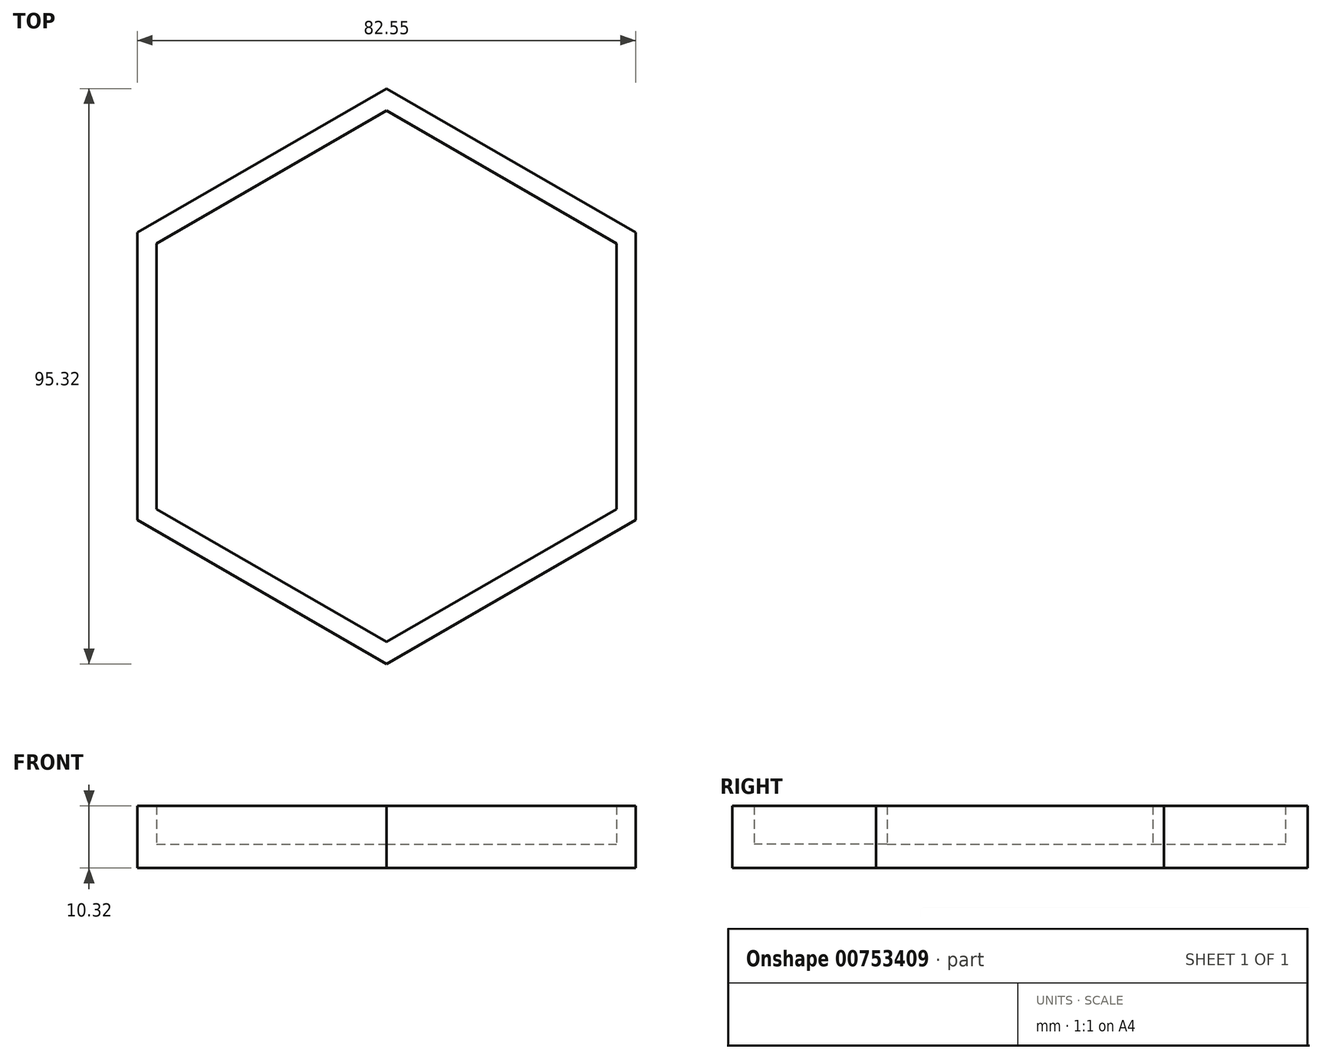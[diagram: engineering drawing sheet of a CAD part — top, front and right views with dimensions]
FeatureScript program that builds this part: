
annotation { "Feature Type Name" : "Feature", "Feature Type Description" : "" }
export const myFeature = defineFeature(function(context is Context, id is Id, definition is map)
    precondition{}
    {
        {
            var Q0;
            Q0=qCreatedBy(makeId("Top.planeOp"),FACE);
            var sketch = newSketch(context, id + "F0", { "sketchPlane" : qUnion([Q0])});
            skCircle(sketch, "E0.cCircle", {"center": v(0, 0) * mm, "radius": 41.28 * mm, "construction": true});
            skLineSegment(sketch, "E0.0", {"start": v(-41.28, -23.83) * mm, "end": v(-41.28, 23.83) * mm});
            skLineSegment(sketch, "E0.1", {"start": v(-41.28, 23.83) * mm, "end": v(0, 47.66) * mm});
            skLineSegment(sketch, "E0.2", {"start": v(0, 47.66) * mm, "end": v(41.28, 23.83) * mm});
            skLineSegment(sketch, "E0.3", {"start": v(41.27, 23.83) * mm, "end": v(41.28, -23.83) * mm});
            skLineSegment(sketch, "E0.4", {"start": v(41.28, -23.83) * mm, "end": v(0, -47.66) * mm});
            skLineSegment(sketch, "E0.5", {"start": v(0, -47.66) * mm, "end": v(-41.27, -23.83) * mm});
            skPoint(sketch, "E0.0.midPoint", {"position": v(-41.28, 0) * mm});
            skSolve(sketch);
        }
        {
            var Q0;
            Q0=makeQuery(id+"F0.imprint","IMPRINT",FACE,{"disambiguationData":[TD([[makeQuery(id+"F0.imprint","IMPRINT",EDGE,{"derivedFrom":sQuery(id+"F0.wireOp",EDGE,"E0.0")}),-1.0]])]});
            extrude(context, id + "F1", {"entities" : qUnion([Q0]), "depth" : 3.97 * mm, "offsetDistance" : 25.4 * mm});
        }
        {
            var Q0;
            Q0=makeQuery(id+"F1.opExtrude","CAP_FACE",FACE,{"disambiguationData":[OSD([sQuery(id+"F0.wireOp",EDGE,"E0.0"),sQuery(id+"F0.wireOp",EDGE,"E0.1"),sQuery(id+"F0.wireOp",EDGE,"E0.2"),sQuery(id+"F0.wireOp",EDGE,"E0.3"),sQuery(id+"F0.wireOp",EDGE,"E0.4"),sQuery(id+"F0.wireOp",EDGE,"E0.5")])],"isStart":false});
            var sketch = newSketch(context, id + "F2", { "sketchPlane" : qUnion([Q0])});
            skCircle(sketch, "E1.cCircle", {"center": v(0, 0) * mm, "radius": 41.28 * mm, "construction": true});
            skLineSegment(sketch, "E1.0", {"start": v(-41.28, -23.83) * mm, "end": v(-41.28, 23.83) * mm});
            skLineSegment(sketch, "E1.1", {"start": v(-41.28, 23.83) * mm, "end": v(0, 47.66) * mm});
            skLineSegment(sketch, "E1.2", {"start": v(0, 47.66) * mm, "end": v(41.28, 23.83) * mm});
            skLineSegment(sketch, "E1.3", {"start": v(41.27, 23.83) * mm, "end": v(41.28, -23.83) * mm});
            skLineSegment(sketch, "E1.4", {"start": v(41.28, -23.83) * mm, "end": v(0, -47.66) * mm});
            skLineSegment(sketch, "E1.5", {"start": v(0, -47.66) * mm, "end": v(-41.28, -23.83) * mm});
            skPoint(sketch, "E1.0.midPoint", {"position": v(-41.28, 0) * mm});
            skLineSegment(sketch, "E2.0", {"start": v(-38.1, -22) * mm, "end": v(-38.1, 22) * mm});
            skLineSegment(sketch, "E2.1", {"start": v(0, 44) * mm, "end": v(38.1, 22) * mm});
            skLineSegment(sketch, "E2.2", {"start": v(38.1, 22) * mm, "end": v(38.1, -22) * mm});
            skLineSegment(sketch, "E2.3", {"start": v(-38.1, 22) * mm, "end": v(0, 44) * mm});
            skLineSegment(sketch, "E2.4", {"start": v(38.1, -22) * mm, "end": v(0, -44) * mm});
            skLineSegment(sketch, "E2.5", {"start": v(0, -44) * mm, "end": v(-38.1, -22) * mm});
            skSolve(sketch);
        }
        {
            var Q0;
            Q0 = qSketchRegion(id + "F2", true);
            extrude(context, id + "F3", {"entities" : qUnion([Q0]), "operationType" : NewBodyOperationType.ADD, "depth" : 6.35 * mm, "offsetDistance" : 25.4 * mm});
        }
    });
